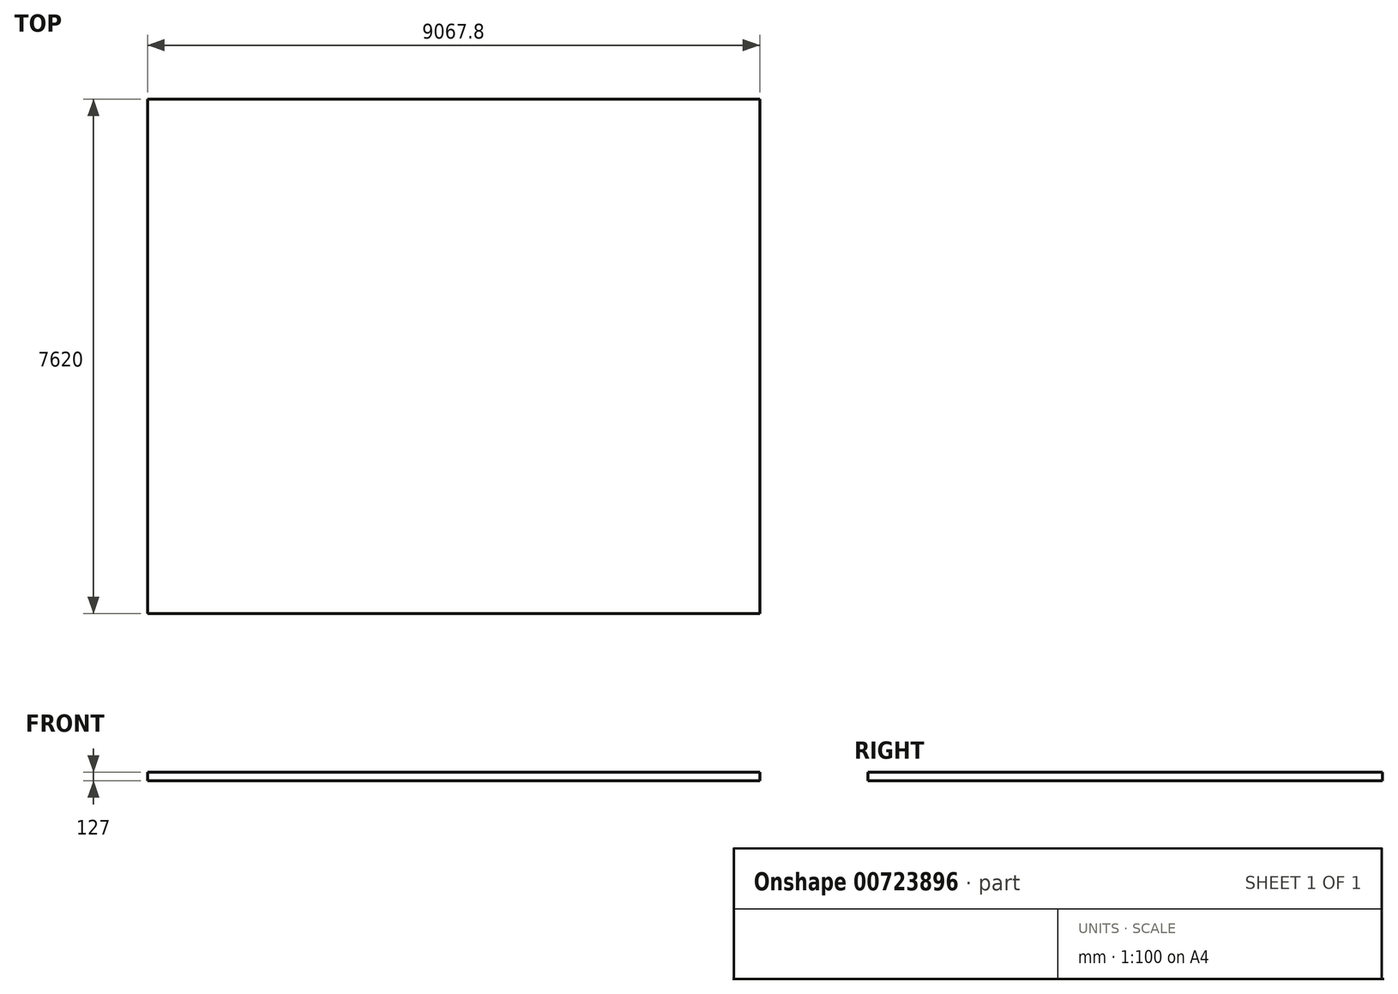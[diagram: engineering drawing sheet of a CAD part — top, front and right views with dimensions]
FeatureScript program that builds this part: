
annotation { "Feature Type Name" : "Feature", "Feature Type Description" : "" }
export const myFeature = defineFeature(function(context is Context, id is Id, definition is map)
    precondition{}
    {
        {
            var Q0;
            Q0=qCreatedBy(makeId("Top.planeOp"),FACE);
            var sketch = newSketch(context, id + "F0", { "sketchPlane" : qUnion([Q0])});
            skLineSegment(sketch, "E0.bottom", {"start": v(4533.9, 3810) * mm, "end": v(-4533.9, 3810) * mm});
            skLineSegment(sketch, "E0.top", {"start": v(4533.9, -3810) * mm, "end": v(-4533.9, -3810) * mm});
            skLineSegment(sketch, "E0.left", {"start": v(4533.9, 3810) * mm, "end": v(4533.9, -3810) * mm});
            skLineSegment(sketch, "E0.right", {"start": v(-4533.9, 3810) * mm, "end": v(-4533.9, -3810) * mm});
            skPoint(sketch, "E0.middle", {"position": v(0, 0) * mm});
            skSolve(sketch);
        }
        {
            var Q0;
            Q0=makeQuery(id+"F0.imprint","IMPRINT",FACE,{"disambiguationData":[TD([[makeQuery(id+"F0.imprint","IMPRINT",EDGE,{"derivedFrom":sQuery(id+"F0.wireOp",EDGE,"E0.bottom")}),1.0]])]});
            extrude(context, id + "F1", {"entities" : qUnion([Q0]), "oppositeDirection" : true, "depth" : 127 * mm, "offsetDistance" : 25.4 * mm});
        }
    });
